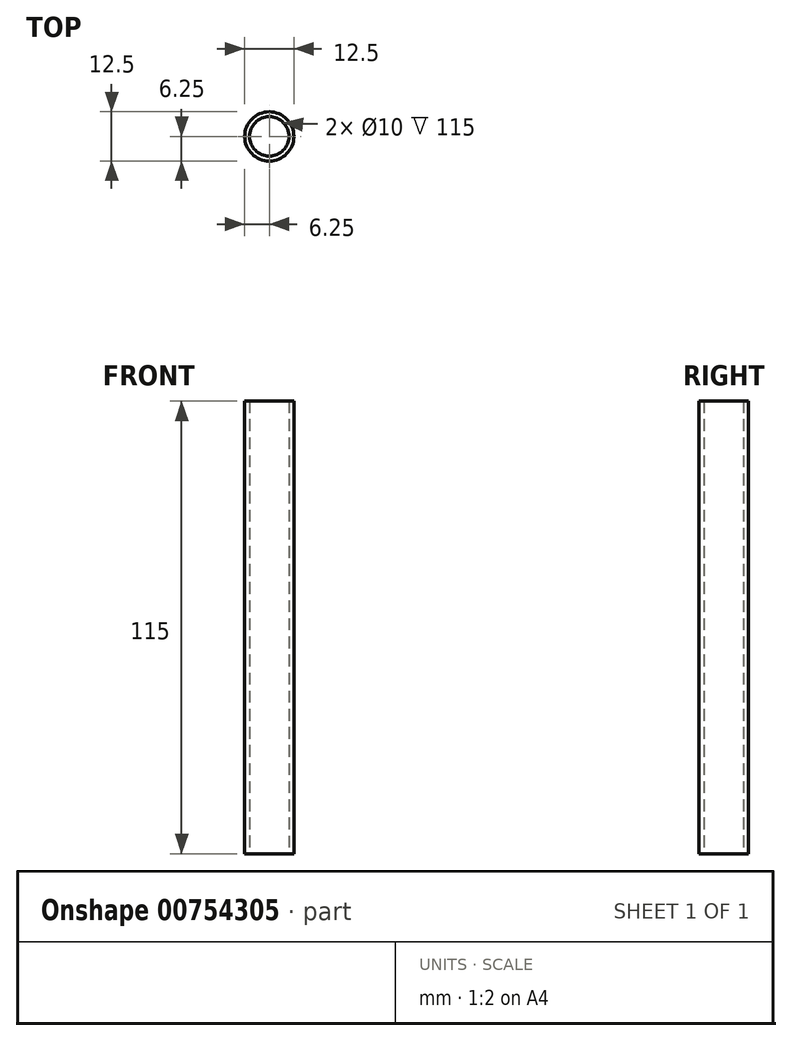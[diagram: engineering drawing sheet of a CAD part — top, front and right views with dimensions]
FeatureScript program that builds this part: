
annotation { "Feature Type Name" : "Feature", "Feature Type Description" : "" }
export const myFeature = defineFeature(function(context is Context, id is Id, definition is map)
    precondition{}
    {
        {
            var Q0;
            Q0=qCreatedBy(makeId("Top.planeOp"),FACE);
            var sketch = newSketch(context, id + "F0", { "sketchPlane" : qUnion([Q0])});
            skCircle(sketch, "E0", {"center": v(0, 0) * mm, "radius": 6.25 * mm});
            skCircle(sketch, "E1", {"center": v(0, 0) * mm, "radius": 5 * mm});
            skSolve(sketch);
        }
        {
            var Q0;
            Q0=makeQuery(id+"F0.imprint","IMPRINT",FACE,{"disambiguationData":[TD([[makeQuery(id+"F0.imprint","IMPRINT",EDGE,{"derivedFrom":sQuery(id+"F0.wireOp",EDGE,"E0")}),1.0]])]});
            extrude(context, id + "F1", {"entities" : qUnion([Q0]), "depth" : 115 * mm, "offsetDistance" : 25 * mm});
        }
    });
